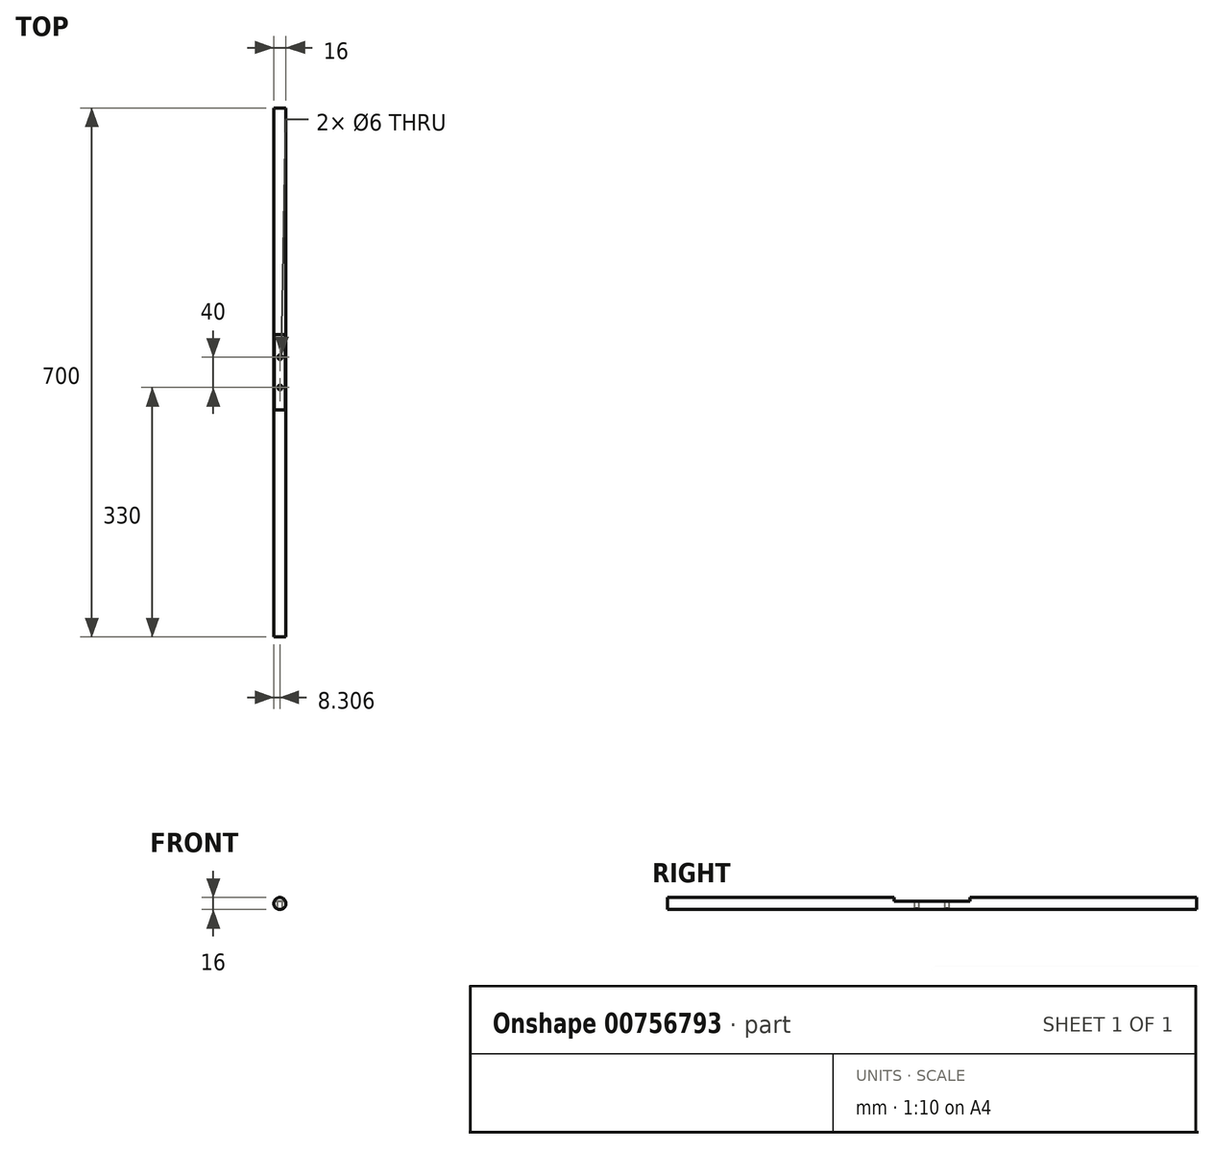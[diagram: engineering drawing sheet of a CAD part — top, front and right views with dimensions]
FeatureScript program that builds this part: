
annotation { "Feature Type Name" : "Feature", "Feature Type Description" : "" }
export const myFeature = defineFeature(function(context is Context, id is Id, definition is map)
    precondition{}
    {
        {
            var Q0;
            Q0=qCreatedBy(makeId("Front.planeOp"),FACE);
            var sketch = newSketch(context, id + "F0", { "sketchPlane" : qUnion([Q0])});
            skCircle(sketch, "E0", {"center": v(-65.65, 44.17) * mm, "radius": 8 * mm});
            skSolve(sketch);
        }
        {
            var Q0;
            Q0 = qSketchRegion(id + "F0", true);
            extrude(context, id + "F1", {"entities" : qUnion([Q0]), "depth" : 700 * mm, "offsetDistance" : 25 * mm});
        }
        {
            var Q0;
            Q0=qCreatedBy(makeId("Right.planeOp"),FACE);
            var sketch = newSketch(context, id + "F2", { "sketchPlane" : qUnion([Q0])});
            skLineSegment(sketch, "E1.bottom", {"start": v(-400, 52.5) * mm, "end": v(-300, 52.5) * mm});
            skLineSegment(sketch, "E1.top", {"start": v(-400, 47.5) * mm, "end": v(-300, 47.5) * mm});
            skLineSegment(sketch, "E1.left", {"start": v(-400, 52.5) * mm, "end": v(-400, 47.5) * mm});
            skLineSegment(sketch, "E1.right", {"start": v(-300, 52.5) * mm, "end": v(-300, 47.5) * mm});
            skSolve(sketch);
        }
        {
            var Q0;
            Q0 = qSketchRegion(id + "F2", true);
            extrude(context, id + "F3", {"entities" : qUnion([Q0]), "operationType" : NewBodyOperationType.REMOVE, "oppositeDirection" : true, "depth" : 88 * mm, "offsetDistance" : 25 * mm});
        }
        {
            var Q0;
            Q0=makeQuery(id+"F3.boolean.opBoolean","COPY",FACE,{"derivedFrom":makeQuery(id+"F3.opExtrude","SWEPT_FACE",FACE,{"disambiguationData":[OSD([sQuery(id+"F2.wireOp",EDGE,"E1.top")])]})});
            var sketch = newSketch(context, id + "F4", { "sketchPlane" : qUnion([Q0])});
            skCircle(sketch, "E2", {"center": v(-65.34, -370) * mm, "radius": 3 * mm});
            skCircle(sketch, "E3", {"center": v(-65.34, -330) * mm, "radius": 3 * mm});
            skSolve(sketch);
        }
        {
            var Q0;
            Q0=makeQuery(id+"F4.imprint","IMPRINT",FACE,{"disambiguationData":[TD([[makeQuery(id+"F4.imprint","IMPRINT",EDGE,{"derivedFrom":sQuery(id+"F4.wireOp",EDGE,"E2")}),1.0]])]});
            var Q1;
            Q1=makeQuery(id+"F4.imprint","IMPRINT",FACE,{"disambiguationData":[TD([[makeQuery(id+"F4.imprint","IMPRINT",EDGE,{"derivedFrom":sQuery(id+"F4.wireOp",EDGE,"E3")}),1.0]])]});
            var Q2;
            Q2=sQuery(id+"F4.wireOp",EDGE,"E3");
            var Q3;
            Q3=sQuery(id+"F4.wireOp",EDGE,"E2");
            extrude(context, id + "F5", {"entities" : qUnion([Q0, Q1]), "operationType" : NewBodyOperationType.REMOVE, "surfaceEntities" : qUnion([Q2, Q3]), "oppositeDirection" : true, "depth" : 15 * mm, "offsetDistance" : 25 * mm});
        }
    });
